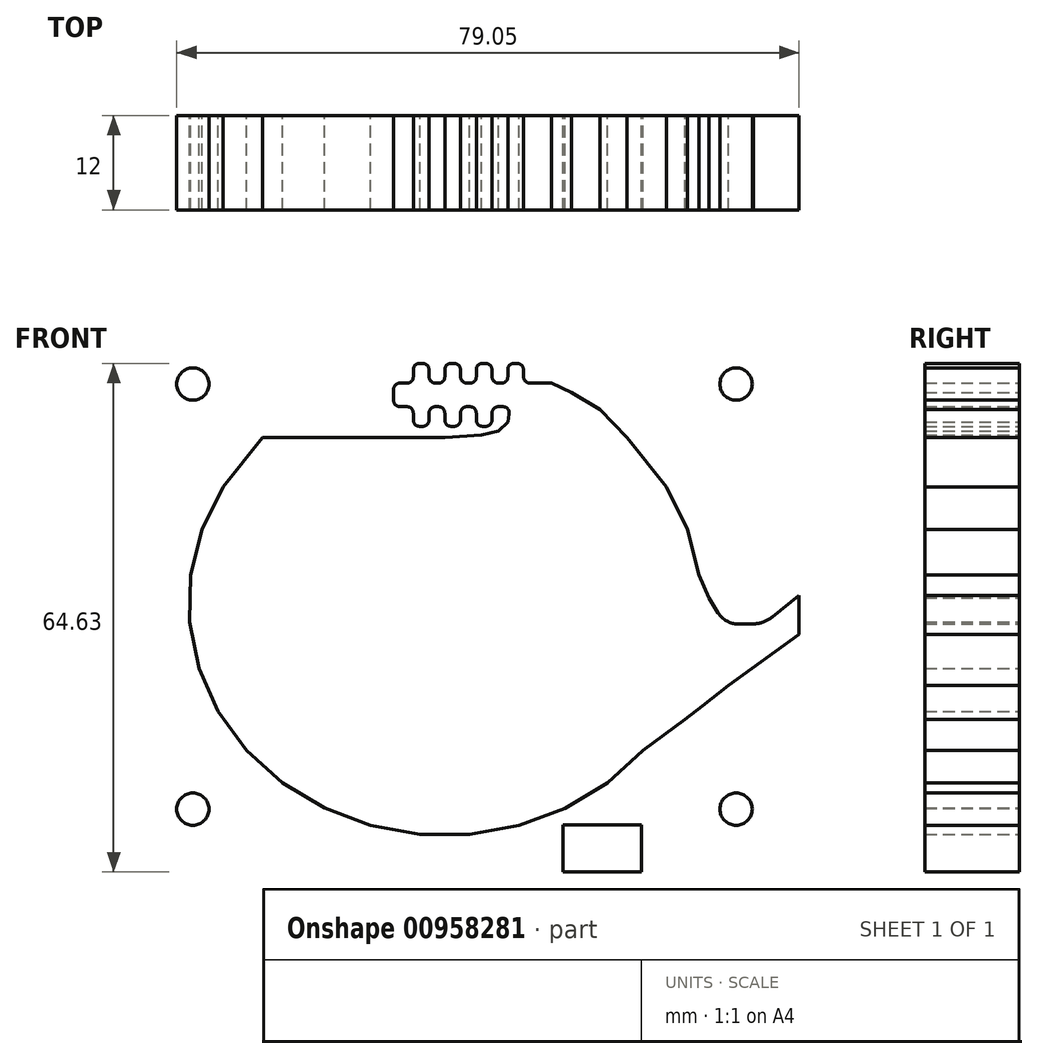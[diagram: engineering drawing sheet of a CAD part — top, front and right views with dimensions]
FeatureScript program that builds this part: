
annotation { "Feature Type Name" : "Feature", "Feature Type Description" : "" }
export const myFeature = defineFeature(function(context is Context, id is Id, definition is map)
    precondition{}
    {
        {
            var Q0;
            Q0=qCreatedBy(makeId("Front.planeOp"),FACE);
            var sketch = newSketch(context, id + "F0", { "sketchPlane" : qUnion([Q0])});
            skLineSegment(sketch, "E0", {"start": v(-23.9, 16.24) * mm, "end": v(-20.75, 20.19) * mm});
            skLineSegment(sketch, "E1", {"start": v(-26.12, 11.8) * mm, "end": v(-23.9, 16.23) * mm});
            skLineSegment(sketch, "E2", {"start": v(-27.3, 7.06) * mm, "end": v(-26.12, 11.8) * mm});
            skLineSegment(sketch, "E3", {"start": v(-24.42, -7.1) * mm, "end": v(-21.45, -11.16) * mm});
            skLineSegment(sketch, "E4", {"start": v(-21.45, -11.16) * mm, "end": v(-17.64, -14.62) * mm});
            skLineSegment(sketch, "E5", {"start": v(-2.72, -20.19) * mm, "end": v(2.72, -20.19) * mm});
            skLineSegment(sketch, "E6", {"start": v(8.09, -19.23) * mm, "end": v(13.1, -17.35) * mm});
            skLineSegment(sketch, "E7", {"start": v(17.64, -14.62) * mm, "end": v(21.45, -11.16) * mm});
            skLineSegment(sketch, "E8", {"start": v(24.43, -7.08) * mm, "end": v(26.44, -2.58) * mm});
            skLineSegment(sketch, "E9", {"start": v(27.3, 7.05) * mm, "end": v(27.41, 2.2) * mm});
            skLineSegment(sketch, "E10", {"start": v(26.12, 11.8) * mm, "end": v(27.3, 7.05) * mm});
            skLineSegment(sketch, "E11", {"start": v(23.9, 16.22) * mm, "end": v(26.12, 11.8) * mm});
            skLineSegment(sketch, "E12", {"start": v(-17.64, -14.62) * mm, "end": v(-13.11, -17.35) * mm});
            skLineSegment(sketch, "E13", {"start": v(-13.11, -17.35) * mm, "end": v(-13.11, -17.35) * mm});
            skLineSegment(sketch, "E14", {"start": v(-13.11, -17.35) * mm, "end": v(-8.08, -19.23) * mm});
            skLineSegment(sketch, "E15", {"start": v(-8.08, -19.23) * mm, "end": v(-8.08, -19.23) * mm});
            skLineSegment(sketch, "E16", {"start": v(-8.08, -19.23) * mm, "end": v(-8.08, -19.23) * mm});
            skLineSegment(sketch, "E17", {"start": v(-8.08, -19.23) * mm, "end": v(-8.08, -19.23) * mm});
            skLineSegment(sketch, "E18", {"start": v(-8.08, -19.23) * mm, "end": v(-2.73, -20.19) * mm});
            skLineSegment(sketch, "E19", {"start": v(-2.73, -20.19) * mm, "end": v(-2.72, -20.19) * mm});
            skLineSegment(sketch, "E20", {"start": v(-2.73, -20.19) * mm, "end": v(-2.73, -20.19) * mm});
            skLineSegment(sketch, "E21", {"start": v(2.72, -20.19) * mm, "end": v(8.09, -19.23) * mm});
            skLineSegment(sketch, "E22", {"start": v(13.1, -17.35) * mm, "end": v(17.64, -14.62) * mm});
            skLineSegment(sketch, "E23", {"start": v(21.45, -11.16) * mm, "end": v(24.43, -7.08) * mm});
            skLineSegment(sketch, "E24", {"start": v(26.44, -2.58) * mm, "end": v(27.41, 2.2) * mm});
            skLineSegment(sketch, "E25", {"start": v(27.3, 7.05) * mm, "end": v(27.3, 7.05) * mm});
            skLineSegment(sketch, "E26", {"start": v(26.12, 11.8) * mm, "end": v(26.12, 11.8) * mm});
            skLineSegment(sketch, "E27", {"start": v(23.9, 16.23) * mm, "end": v(23.9, 16.22) * mm});
            skLineSegment(sketch, "E28", {"start": v(23.9, 16.23) * mm, "end": v(23.9, 16.23) * mm});
            skLineSegment(sketch, "E29", {"start": v(20.75, 20.18) * mm, "end": v(23.9, 16.23) * mm});
            skLineSegment(sketch, "E30", {"start": v(-23.9, 16.23) * mm, "end": v(-23.9, 16.24) * mm});
            skLineSegment(sketch, "E31", {"start": v(-23.9, 16.23) * mm, "end": v(-23.9, 16.23) * mm});
            skLineSegment(sketch, "E32", {"start": v(-26.12, 11.8) * mm, "end": v(-26.12, 11.8) * mm});
            skLineSegment(sketch, "E33", {"start": v(-27.3, 7.05) * mm, "end": v(-27.3, 7.05) * mm});
            skLineSegment(sketch, "E34", {"start": v(-27.3, 7.05) * mm, "end": v(-27.3, 7.06) * mm});
            skLineSegment(sketch, "E35", {"start": v(-27.41, 2.2) * mm, "end": v(-27.3, 7.05) * mm});
            skLineSegment(sketch, "E36", {"start": v(-27.41, 2.2) * mm, "end": v(-27.41, 2.2) * mm});
            skLineSegment(sketch, "E37", {"start": v(-27.41, 2.2) * mm, "end": v(-26.44, -2.58) * mm});
            skLineSegment(sketch, "E38", {"start": v(-26.44, -2.58) * mm, "end": v(-26.44, -2.58) * mm});
            skLineSegment(sketch, "E39", {"start": v(-26.44, -2.58) * mm, "end": v(-24.42, -7.1) * mm});
            skLineSegment(sketch, "E40", {"start": v(-20.75, 20.19) * mm, "end": v(20.75, 20.18) * mm});
            skSolve(sketch);
        }
        {
            var Q0;
            Q0=qCreatedBy(makeId("Front.planeOp"),FACE);
            var sketch = newSketch(context, id + "F1", { "sketchPlane" : qUnion([Q0])});
            skLineSegment(sketch, "E41.bottom", {"start": v(-40, -30) * mm, "end": v(45, -30) * mm});
            skLineSegment(sketch, "E41.top", {"start": v(-40, 40) * mm, "end": v(45, 40) * mm});
            skLineSegment(sketch, "E41.left", {"start": v(-40, -30) * mm, "end": v(-40, 40) * mm});
            skLineSegment(sketch, "E41.right", {"start": v(45, -30) * mm, "end": v(45, 40) * mm});
            skSolve(sketch);
        }
        {
            var Q0;
            Q0=qCreatedBy(makeId("Front.planeOp"),FACE);
            var sketch = newSketch(context, id + "F2", { "sketchPlane" : qUnion([Q0])});
            skLineSegment(sketch, "E42.0", {"start": v(28.78, -9.6) * mm, "end": v(31.23, -4.12) * mm});
            skLineSegment(sketch, "E42.1", {"start": v(-32.42, 1.75) * mm, "end": v(-31.23, -4.11) * mm});
            skLineSegment(sketch, "E42.2", {"start": v(-32.42, 1.75) * mm, "end": v(-32.29, 7.73) * mm});
            skLineSegment(sketch, "E42.3", {"start": v(-32.29, 7.73) * mm, "end": v(-30.84, 13.53) * mm});
            skLineSegment(sketch, "E42.4", {"start": v(-30.84, 13.53) * mm, "end": v(-28.14, 18.93) * mm});
            skLineSegment(sketch, "E42.5", {"start": v(-28.14, 18.93) * mm, "end": v(-23.16, 25.19) * mm});
            skLineSegment(sketch, "E42.6", {"start": v(-23.16, 25.19) * mm, "end": v(23.16, 25.18) * mm});
            skLineSegment(sketch, "E42.7", {"start": v(32.3, 7.72) * mm, "end": v(32.42, 1.76) * mm});
            skLineSegment(sketch, "E42.8", {"start": v(30.84, 13.53) * mm, "end": v(32.3, 7.72) * mm});
            skLineSegment(sketch, "E42.9", {"start": v(28.15, 18.93) * mm, "end": v(30.84, 13.53) * mm});
            skLineSegment(sketch, "E42.10", {"start": v(23.16, 25.18) * mm, "end": v(28.15, 18.93) * mm});
            skLineSegment(sketch, "E42.11", {"start": v(-31.23, -4.11) * mm, "end": v(-28.77, -9.62) * mm});
            skLineSegment(sketch, "E42.12", {"start": v(31.23, -4.12) * mm, "end": v(32.42, 1.76) * mm});
            skLineSegment(sketch, "E42.13", {"start": v(-28.77, -9.62) * mm, "end": v(-25.19, -14.52) * mm});
            skLineSegment(sketch, "E42.14", {"start": v(-25.19, -14.52) * mm, "end": v(-20.64, -18.65) * mm});
            skLineSegment(sketch, "E42.15", {"start": v(-20.64, -18.65) * mm, "end": v(-15.3, -21.87) * mm});
            skLineSegment(sketch, "E42.16", {"start": v(-15.3, -21.87) * mm, "end": v(-9.4, -24.07) * mm});
            skLineSegment(sketch, "E42.17", {"start": v(-9.4, -24.07) * mm, "end": v(-3.16, -25.19) * mm});
            skLineSegment(sketch, "E42.18", {"start": v(-3.16, -25.19) * mm, "end": v(3.16, -25.19) * mm});
            skLineSegment(sketch, "E42.19", {"start": v(3.16, -25.19) * mm, "end": v(9.42, -24.07) * mm});
            skLineSegment(sketch, "E42.20", {"start": v(9.42, -24.07) * mm, "end": v(15.3, -21.88) * mm});
            skLineSegment(sketch, "E42.21", {"start": v(15.3, -21.88) * mm, "end": v(20.64, -18.65) * mm});
            skLineSegment(sketch, "E42.22", {"start": v(20.64, -18.65) * mm, "end": v(25.18, -14.53) * mm});
            skLineSegment(sketch, "E42.23", {"start": v(25.18, -14.53) * mm, "end": v(28.78, -9.6) * mm});
            skLineSegment(sketch, "E43.bottom", {"start": v(-40, 40) * mm, "end": v(45, 40) * mm});
            skLineSegment(sketch, "E43.top", {"start": v(-40, -30) * mm, "end": v(22, -30) * mm});
            skLineSegment(sketch, "E43.left", {"start": v(-40, 40) * mm, "end": v(-40, -30) * mm});
            skLineSegment(sketch, "E43.right", {"start": v(45, 40) * mm, "end": v(45, -30) * mm});
            skCircle(sketch, "E44", {"center": v(-32, -22) * mm, "radius": 2.05 * mm});
            skCircle(sketch, "E45.MirrorC", {"center": v(37, -22) * mm, "radius": 2.05 * mm});
            skLineSegment(sketch, "E46.top", {"start": v(22, -24) * mm, "end": v(32, -24) * mm});
            skLineSegment(sketch, "E46.left", {"start": v(22, -30) * mm, "end": v(22, -24) * mm});
            skLineSegment(sketch, "E46.right", {"start": v(32, -30) * mm, "end": v(32, -24) * mm});
            skLineSegment(sketch, "E47.trimOffspring", {"start": v(32, -30) * mm, "end": v(45, -30) * mm});
            skCircle(sketch, "E48", {"center": v(-32, 32) * mm, "radius": 2.05 * mm});
            skCircle(sketch, "E49.MirrorC", {"center": v(37, 32) * mm, "radius": 2.05 * mm});
            skSolve(sketch);
        }
        {
            var Q0;
            Q0=qCreatedBy(makeId("Front.planeOp"),FACE);
            var sketch = newSketch(context, id + "F3", { "sketchPlane" : qUnion([Q0])});
            skLineSegment(sketch, "E50.bottom", {"start": v(-40, -30) * mm, "end": v(45, -30) * mm});
            skLineSegment(sketch, "E50.top", {"start": v(-40, 40) * mm, "end": v(45, 40) * mm});
            skLineSegment(sketch, "E50.left", {"start": v(-40, -30) * mm, "end": v(-40, 40) * mm});
            skLineSegment(sketch, "E50.right", {"start": v(45, -30) * mm, "end": v(45, 40) * mm});
            skCircle(sketch, "E51", {"center": v(-32, -22) * mm, "radius": 2.05 * mm});
            skCircle(sketch, "E52", {"center": v(37, -22) * mm, "radius": 2.05 * mm});
            skCircle(sketch, "E53", {"center": v(-32, 32) * mm, "radius": 2.05 * mm});
            skCircle(sketch, "E54", {"center": v(37, 32) * mm, "radius": 2.05 * mm});
            skSolve(sketch);
        }
        {
            var Q0;
            Q0=qCreatedBy(makeId("Front.planeOp"),FACE);
            var sketch = newSketch(context, id + "F4", { "sketchPlane" : qUnion([Q0])});
            skLineSegment(sketch, "E55.1", {"start": v(-32.42, 1.75) * mm, "end": v(-31.23, -4.11) * mm});
            skLineSegment(sketch, "E55.2", {"start": v(-32.42, 1.75) * mm, "end": v(-32.29, 7.73) * mm});
            skLineSegment(sketch, "E55.3", {"start": v(-32.29, 7.73) * mm, "end": v(-30.84, 13.53) * mm});
            skLineSegment(sketch, "E55.4", {"start": v(-30.84, 13.53) * mm, "end": v(-28.14, 18.93) * mm});
            skLineSegment(sketch, "E55.5", {"start": v(-28.14, 18.93) * mm, "end": v(-23.16, 25.19) * mm});
            skLineSegment(sketch, "E55.9", {"start": v(28.15, 18.93) * mm, "end": v(30.84, 13.53) * mm});
            skLineSegment(sketch, "E55.11", {"start": v(-31.23, -4.11) * mm, "end": v(-28.77, -9.62) * mm});
            skLineSegment(sketch, "E55.13", {"start": v(-28.77, -9.62) * mm, "end": v(-25.19, -14.52) * mm});
            skLineSegment(sketch, "E55.14", {"start": v(-25.19, -14.52) * mm, "end": v(-20.64, -18.65) * mm});
            skLineSegment(sketch, "E55.15", {"start": v(-20.64, -18.65) * mm, "end": v(-15.3, -21.87) * mm});
            skLineSegment(sketch, "E55.16", {"start": v(-15.3, -21.87) * mm, "end": v(-9.4, -24.07) * mm});
            skLineSegment(sketch, "E55.17", {"start": v(-9.4, -24.07) * mm, "end": v(-3.16, -25.19) * mm});
            skLineSegment(sketch, "E55.18", {"start": v(-3.16, -25.19) * mm, "end": v(3.16, -25.19) * mm});
            skLineSegment(sketch, "E55.19", {"start": v(3.16, -25.19) * mm, "end": v(9.42, -24.07) * mm});
            skLineSegment(sketch, "E55.20", {"start": v(15.3, -21.88) * mm, "end": v(9.42, -24.07) * mm});
            skLineSegment(sketch, "E55.21", {"start": v(15.3, -21.88) * mm, "end": v(20.64, -18.65) * mm});
            skLineSegment(sketch, "E55.22", {"start": v(20.64, -18.65) * mm, "end": v(25.18, -14.53) * mm});
            skLineSegment(sketch, "E56.bottom", {"start": v(-40, 40) * mm, "end": v(45, 40) * mm});
            skLineSegment(sketch, "E56.top", {"start": v(-40, -30) * mm, "end": v(15, -30) * mm});
            skLineSegment(sketch, "E56.left", {"start": v(-40, 40) * mm, "end": v(-40, -30) * mm});
            skLineSegment(sketch, "E56.right", {"start": v(45, 40) * mm, "end": v(45, 5.17) * mm});
            skPoint(sketch, "E57", {"position": v(2.5, 40) * mm});
            skCircle(sketch, "E58", {"center": v(-32, -22) * mm, "radius": 2.05 * mm});
            skCircle(sketch, "E59.MirrorC", {"center": v(37, -22) * mm, "radius": 2.05 * mm});
            skLineSegment(sketch, "E60.top", {"start": v(15, -24) * mm, "end": v(25, -24) * mm});
            skLineSegment(sketch, "E60.left", {"start": v(15, -30) * mm, "end": v(15, -24) * mm});
            skLineSegment(sketch, "E60.right", {"start": v(25, -30) * mm, "end": v(25, -24) * mm});
            skLineSegment(sketch, "E61.trimOffspring", {"start": v(25, -30) * mm, "end": v(45, -30) * mm});
            skCircle(sketch, "E62", {"center": v(-32, 32) * mm, "radius": 2.05 * mm});
            skCircle(sketch, "E63.MirrorC", {"center": v(37, 32) * mm, "radius": 2.05 * mm});
            skLineSegment(sketch, "E64", {"start": v(-23.16, 25.19) * mm, "end": v(0, 25.19) * mm});
            skLineSegment(sketch, "E65", {"start": v(0, 25.19) * mm, "end": v(4.68, 25.52) * mm});
            skLineSegment(sketch, "E66", {"start": v(4.68, 25.52) * mm, "end": v(6.82, 26.04) * mm});
            skLineSegment(sketch, "E67", {"start": v(10.99, 32.13) * mm, "end": v(13.55, 32.13) * mm});
            skLineSegment(sketch, "E68", {"start": v(13.55, 32.13) * mm, "end": v(16.11, 30.96) * mm});
            skLineSegment(sketch, "E69", {"start": v(16.11, 30.96) * mm, "end": v(19.74, 28.78) * mm});
            skLineSegment(sketch, "E70", {"start": v(23.16, 25.18) * mm, "end": v(28.15, 18.93) * mm});
            skLineSegment(sketch, "E71", {"start": v(19.74, 28.78) * mm, "end": v(23.16, 25.18) * mm});
            skLineSegment(sketch, "E72", {"start": v(33.55, 4.85) * mm, "end": v(32.3, 7.72) * mm});
            skLineSegment(sketch, "E73", {"start": v(32.3, 7.72) * mm, "end": v(30.84, 13.53) * mm});
            skLineSegment(sketch, "E74", {"start": v(36.03, -6.3) * mm, "end": v(32.73, -8.86) * mm});
            skLineSegment(sketch, "E75", {"start": v(32.73, -8.86) * mm, "end": v(30.53, -10.58) * mm});
            skLineSegment(sketch, "E76", {"start": v(30.53, -10.58) * mm, "end": v(25.18, -14.53) * mm});
            skLineSegment(sketch, "E77", {"start": v(6.82, 26.04) * mm, "end": v(8, 27.2) * mm});
            skLineSegment(sketch, "E78", {"start": v(8, 27.2) * mm, "end": v(8.18, 28.2) * mm});
            skLineSegment(sketch, "E79.bottom", {"start": v(4.8, 26.63) * mm, "end": v(5.2, 26.63) * mm});
            skLineSegment(sketch, "E79.top", {"start": v(4.8, 34.63) * mm, "end": v(5.2, 34.63) * mm});
            skLineSegment(sketch, "E79.left", {"start": v(4, 27.43) * mm, "end": v(4, 28.33) * mm});
            skLineSegment(sketch, "E79.right", {"start": v(6, 27.43) * mm, "end": v(6, 28.33) * mm});
            skLineSegment(sketch, "E80.1.0.0", {"start": v(2, 27.43) * mm, "end": v(2, 28.33) * mm});
            skLineSegment(sketch, "E80.1.0.1", {"start": v(0.8, 26.63) * mm, "end": v(1.2, 26.63) * mm});
            skLineSegment(sketch, "E80.1.0.2", {"start": v(0.8, 34.63) * mm, "end": v(1.2, 34.63) * mm});
            skLineSegment(sketch, "E80.1.0.3", {"start": v(0, 27.43) * mm, "end": v(0, 28.33) * mm});
            skLineSegment(sketch, "E80.2.0.0", {"start": v(-2, 27.43) * mm, "end": v(-2, 28.33) * mm});
            skLineSegment(sketch, "E80.2.0.1", {"start": v(-3.2, 26.63) * mm, "end": v(-2.8, 26.63) * mm});
            skLineSegment(sketch, "E80.2.0.2", {"start": v(-3.2, 34.63) * mm, "end": v(-2.8, 34.63) * mm});
            skLineSegment(sketch, "E80.2.0.3", {"start": v(-4, 27.43) * mm, "end": v(-4, 28.33) * mm});
            skLineSegment(sketch, "E80.direction1", {"start": v(4, 26.63) * mm, "end": v(0, 26.63) * mm, "construction": true});
            skLineSegment(sketch, "E81.bottom", {"start": v(-5.7, 29.13) * mm, "end": v(-4.8, 29.13) * mm});
            skLineSegment(sketch, "E81.top", {"start": v(-5.7, 32.13) * mm, "end": v(-4.8, 32.13) * mm});
            skLineSegment(sketch, "E81.left", {"start": v(-6.5, 29.93) * mm, "end": v(-6.5, 31.33) * mm});
            skLineSegment(sketch, "E82.trimOffspring", {"start": v(-1.2, 32.13) * mm, "end": v(-0.8, 32.13) * mm});
            skLineSegment(sketch, "E83.trimOffspring", {"start": v(-1.2, 29.13) * mm, "end": v(-0.8, 29.13) * mm});
            skLineSegment(sketch, "E84.trimOffspring", {"start": v(-4, 32.93) * mm, "end": v(-4, 33.83) * mm});
            skLineSegment(sketch, "E85.trimOffspring", {"start": v(-2, 32.93) * mm, "end": v(-2, 33.83) * mm});
            skLineSegment(sketch, "E86.trimOffspring", {"start": v(0, 32.93) * mm, "end": v(0, 33.83) * mm});
            skLineSegment(sketch, "E87.trimOffspring", {"start": v(2.8, 32.13) * mm, "end": v(3.2, 32.13) * mm});
            skLineSegment(sketch, "E88.trimOffspring", {"start": v(2.8, 29.13) * mm, "end": v(3.2, 29.13) * mm});
            skLineSegment(sketch, "E89.trimOffspring", {"start": v(2, 32.93) * mm, "end": v(2, 33.83) * mm});
            skLineSegment(sketch, "E90.trimOffspring", {"start": v(4, 32.93) * mm, "end": v(4, 33.83) * mm});
            skLineSegment(sketch, "E91.trimOffspring", {"start": v(6.8, 32.13) * mm, "end": v(7.2, 32.13) * mm});
            skLineSegment(sketch, "E92.trimOffspring", {"start": v(6.8, 29.13) * mm, "end": v(7.39, 29.13) * mm});
            skLineSegment(sketch, "E93.trimOffspring", {"start": v(6, 32.93) * mm, "end": v(6, 33.83) * mm});
            skPoint(sketch, "E94.visualSharp", {"position": v(-4, 34.63) * mm});
            skArc(sketch, "E94.filletArc", {"start": v(-3.2, 34.63) * mm, "mid": v(-3.77, 34.4) * mm, "end": v(-4, 33.83) * mm});
            skPoint(sketch, "E95.visualSharp", {"position": v(-2, 34.63) * mm});
            skArc(sketch, "E95.filletArc", {"start": v(-2, 33.83) * mm, "mid": v(-2.23, 34.4) * mm, "end": v(-2.8, 34.63) * mm});
            skPoint(sketch, "E96.visualSharp", {"position": v(-4, 26.63) * mm});
            skArc(sketch, "E96.filletArc", {"start": v(-4, 27.43) * mm, "mid": v(-3.77, 26.86) * mm, "end": v(-3.2, 26.63) * mm});
            skPoint(sketch, "E97.visualSharp", {"position": v(-2, 26.63) * mm});
            skArc(sketch, "E97.filletArc", {"start": v(-2.8, 26.63) * mm, "mid": v(-2.23, 26.86) * mm, "end": v(-2, 27.43) * mm});
            skPoint(sketch, "E98.visualSharp", {"position": v(-6.5, 29.13) * mm});
            skArc(sketch, "E98.filletArc", {"start": v(-6.5, 29.93) * mm, "mid": v(-6.27, 29.36) * mm, "end": v(-5.7, 29.13) * mm});
            skPoint(sketch, "E99.visualSharp", {"position": v(-6.5, 32.13) * mm});
            skArc(sketch, "E99.filletArc", {"start": v(-5.7, 32.13) * mm, "mid": v(-6.27, 31.9) * mm, "end": v(-6.5, 31.33) * mm});
            skPoint(sketch, "E100.visualSharp", {"position": v(-4, 32.13) * mm});
            skArc(sketch, "E100.filletArc", {"start": v(-4.8, 32.13) * mm, "mid": v(-4.23, 32.36) * mm, "end": v(-4, 32.93) * mm});
            skPoint(sketch, "E101.visualSharp", {"position": v(-4, 29.13) * mm});
            skArc(sketch, "E101.filletArc", {"start": v(-4, 28.33) * mm, "mid": v(-4.23, 28.9) * mm, "end": v(-4.8, 29.13) * mm});
            skPoint(sketch, "E102.visualSharp", {"position": v(-2, 29.13) * mm});
            skArc(sketch, "E102.filletArc", {"start": v(-1.2, 29.13) * mm, "mid": v(-1.77, 28.9) * mm, "end": v(-2, 28.33) * mm});
            skPoint(sketch, "E103.visualSharp", {"position": v(-2, 32.13) * mm});
            skArc(sketch, "E103.filletArc", {"start": v(-2, 32.93) * mm, "mid": v(-1.77, 32.36) * mm, "end": v(-1.2, 32.13) * mm});
            skPoint(sketch, "E104.visualSharp", {"position": v(0, 34.63) * mm});
            skArc(sketch, "E104.filletArc", {"start": v(0.8, 34.63) * mm, "mid": v(0.23, 34.4) * mm, "end": v(0, 33.83) * mm});
            skPoint(sketch, "E105.visualSharp", {"position": v(6, 34.63) * mm});
            skArc(sketch, "E105.filletArc", {"start": v(6, 33.83) * mm, "mid": v(5.77, 34.4) * mm, "end": v(5.2, 34.63) * mm});
            skPoint(sketch, "E106.visualSharp", {"position": v(4, 34.63) * mm});
            skArc(sketch, "E106.filletArc", {"start": v(4.8, 34.63) * mm, "mid": v(4.23, 34.4) * mm, "end": v(4, 33.83) * mm});
            skPoint(sketch, "E107.visualSharp", {"position": v(6, 26.63) * mm});
            skArc(sketch, "E107.filletArc", {"start": v(5.2, 26.63) * mm, "mid": v(5.77, 26.86) * mm, "end": v(6, 27.43) * mm});
            skPoint(sketch, "E108.visualSharp", {"position": v(4, 29.13) * mm});
            skArc(sketch, "E108.filletArc", {"start": v(4, 28.33) * mm, "mid": v(3.77, 28.9) * mm, "end": v(3.2, 29.13) * mm});
            skPoint(sketch, "E109.visualSharp", {"position": v(4, 26.63) * mm});
            skArc(sketch, "E109.filletArc", {"start": v(4, 27.43) * mm, "mid": v(4.23, 26.86) * mm, "end": v(4.8, 26.63) * mm});
            skPoint(sketch, "E110.visualSharp", {"position": v(2, 34.63) * mm});
            skArc(sketch, "E110.filletArc", {"start": v(2, 33.83) * mm, "mid": v(1.77, 34.4) * mm, "end": v(1.2, 34.63) * mm});
            skPoint(sketch, "E111.visualSharp", {"position": v(2, 32.13) * mm});
            skArc(sketch, "E111.filletArc", {"start": v(2, 32.93) * mm, "mid": v(2.23, 32.36) * mm, "end": v(2.8, 32.13) * mm});
            skPoint(sketch, "E112.visualSharp", {"position": v(4, 32.13) * mm});
            skArc(sketch, "E112.filletArc", {"start": v(3.2, 32.13) * mm, "mid": v(3.77, 32.36) * mm, "end": v(4, 32.93) * mm});
            skPoint(sketch, "E113.visualSharp", {"position": v(6, 32.13) * mm});
            skArc(sketch, "E113.filletArc", {"start": v(6, 32.93) * mm, "mid": v(6.23, 32.36) * mm, "end": v(6.8, 32.13) * mm});
            skPoint(sketch, "E114.visualSharp", {"position": v(6, 29.13) * mm});
            skArc(sketch, "E114.filletArc", {"start": v(6.8, 29.13) * mm, "mid": v(6.23, 28.9) * mm, "end": v(6, 28.33) * mm});
            skPoint(sketch, "E115.visualSharp", {"position": v(2, 29.13) * mm});
            skArc(sketch, "E115.filletArc", {"start": v(2.8, 29.13) * mm, "mid": v(2.23, 28.9) * mm, "end": v(2, 28.33) * mm});
            skPoint(sketch, "E116.visualSharp", {"position": v(0, 32.13) * mm});
            skArc(sketch, "E116.filletArc", {"start": v(-0.8, 32.13) * mm, "mid": v(-0.23, 32.36) * mm, "end": v(0, 32.93) * mm});
            skPoint(sketch, "E117.visualSharp", {"position": v(0, 29.13) * mm});
            skArc(sketch, "E117.filletArc", {"start": v(0, 28.33) * mm, "mid": v(-0.23, 28.9) * mm, "end": v(-0.8, 29.13) * mm});
            skPoint(sketch, "E118.visualSharp", {"position": v(0, 26.63) * mm});
            skArc(sketch, "E118.filletArc", {"start": v(0, 27.43) * mm, "mid": v(0.23, 26.86) * mm, "end": v(0.8, 26.63) * mm});
            skPoint(sketch, "E119.visualSharp", {"position": v(2, 26.63) * mm});
            skArc(sketch, "E119.filletArc", {"start": v(1.2, 26.63) * mm, "mid": v(1.77, 26.86) * mm, "end": v(2, 27.43) * mm});
            skPoint(sketch, "E120.visualSharp", {"position": v(8.34, 29.13) * mm});
            skArc(sketch, "E120.filletArc", {"start": v(8.18, 28.2) * mm, "mid": v(8, 28.84) * mm, "end": v(7.39, 29.13) * mm});
            skLineSegment(sketch, "E121.top", {"start": v(8.8, 34.63) * mm, "end": v(9.2, 34.63) * mm});
            skLineSegment(sketch, "E122.trimOffspring", {"start": v(8, 32.93) * mm, "end": v(8, 33.83) * mm});
            skLineSegment(sketch, "E123.trimOffspring", {"start": v(10, 32.93) * mm, "end": v(10, 33.83) * mm});
            skPoint(sketch, "E124.visualSharp", {"position": v(10, 34.63) * mm});
            skArc(sketch, "E124.filletArc", {"start": v(10, 33.83) * mm, "mid": v(9.77, 34.4) * mm, "end": v(9.2, 34.63) * mm});
            skPoint(sketch, "E125.visualSharp", {"position": v(8, 34.63) * mm});
            skArc(sketch, "E125.filletArc", {"start": v(8.8, 34.63) * mm, "mid": v(8.23, 34.4) * mm, "end": v(8, 33.83) * mm});
            skPoint(sketch, "E126.visualSharp", {"position": v(8, 32.13) * mm});
            skArc(sketch, "E126.filletArc", {"start": v(7.2, 32.13) * mm, "mid": v(7.77, 32.36) * mm, "end": v(8, 32.93) * mm});
            skPoint(sketch, "E127.visualSharp", {"position": v(10, 32.13) * mm});
            skArc(sketch, "E127.filletArc", {"start": v(10, 32.93) * mm, "mid": v(10.23, 32.36) * mm, "end": v(10.8, 32.13) * mm});
            skLineSegment(sketch, "E128.trimOffspring", {"start": v(10.8, 32.13) * mm, "end": v(10.99, 32.13) * mm});
            skLineSegment(sketch, "E129", {"start": v(36.03, -6.3) * mm, "end": v(45, 0.17) * mm});
            skLineSegment(sketch, "E130", {"start": v(33.55, 4.85) * mm, "end": v(34.72, 2.95) * mm});
            skLineSegment(sketch, "E131", {"start": v(37.28, 1.52) * mm, "end": v(39.19, 1.52) * mm});
            skLineSegment(sketch, "E132", {"start": v(39.19, 1.52) * mm, "end": v(39.45, 1.54) * mm});
            skLineSegment(sketch, "E133", {"start": v(41.6, 2.42) * mm, "end": v(45, 5.17) * mm});
            skLineSegment(sketch, "E134.trimOffspring", {"start": v(45, 0.17) * mm, "end": v(45, -30) * mm});
            skPoint(sketch, "E135.visualSharp", {"position": v(35.6, 1.52) * mm});
            skArc(sketch, "E135.filletArc", {"start": v(34.72, 2.95) * mm, "mid": v(35.81, 1.9) * mm, "end": v(37.28, 1.52) * mm});
            skPoint(sketch, "E136.visualSharp", {"position": v(40.66, 1.65) * mm});
            skArc(sketch, "E136.filletArc", {"start": v(39.45, 1.54) * mm, "mid": v(40.59, 1.82) * mm, "end": v(41.6, 2.42) * mm});
            skSolve(sketch);
        }
        {
            var Q0;
            Q0 = qSketchRegion(id + "F1", true);
            extrude(context, id + "F5", {"entities" : qUnion([Q0]), "depth" : 12 * mm, "offsetDistance" : 25 * mm});
        }
        {
            var Q0;
            Q0 = qSketchRegion(id + "F4", true);
            var Q1;
            Q1=sQuery(id+"F0.wireOp",EDGE,"E27");
            var Q2;
            Q2=sQuery(id+"F0.wireOp",EDGE,"E28");
            var Q3;
            Q3=sQuery(id+"F0.wireOp",EDGE,"E28");
            var Q4;
            Q4=sQuery(id+"F0.wireOp",EDGE,"E28");
            var Q5;
            Q5 = qConstructionFilter(qBodyType(qCreatedBy(id + "F4" ,EDGE), BodyType.WIRE), ConstructionObject.NO);
            extrude(context, id + "F6", {"entities" : qUnion([Q0]), "operationType" : NewBodyOperationType.REMOVE, "surfaceEntities" : qUnion([Q1, Q2, Q3, Q4, Q5]), "depth" : 62.1 * mm, "offsetDistance" : 25 * mm});
        }
    });
